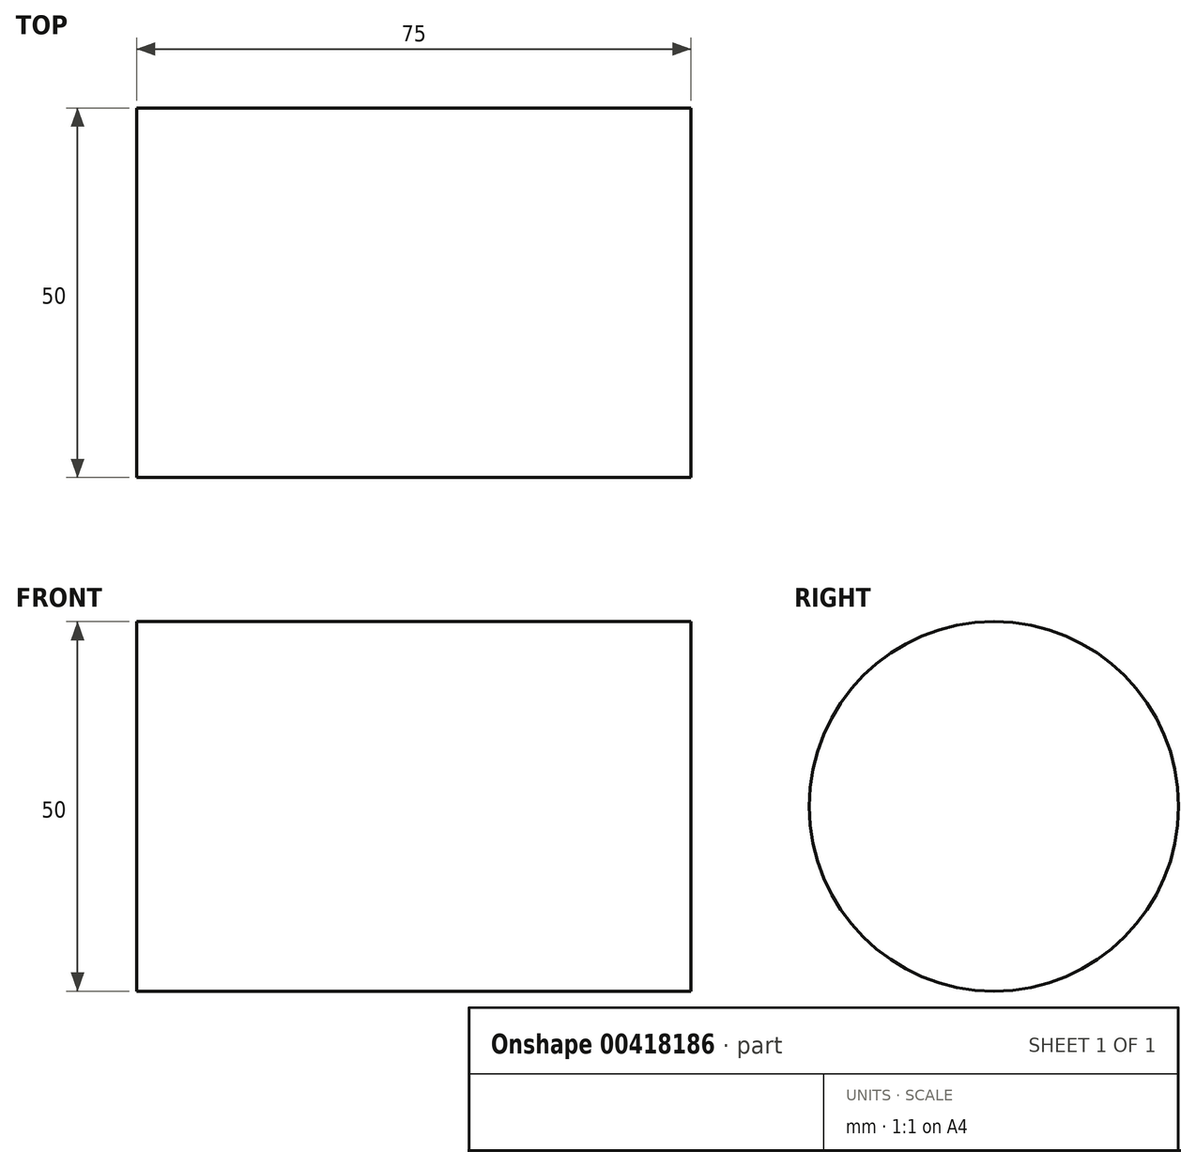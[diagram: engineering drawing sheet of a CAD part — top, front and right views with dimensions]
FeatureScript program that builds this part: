
annotation { "Feature Type Name" : "Feature", "Feature Type Description" : "" }
export const myFeature = defineFeature(function(context is Context, id is Id, definition is map)
    precondition{}
    {
        {
            var Q0;
            Q0=qCreatedBy(makeId("Right.planeOp"),FACE);
            var sketch = newSketch(context, id + "F0", { "sketchPlane" : qUnion([Q0])});
            skCircle(sketch, "E0", {"center": v(0, 0) * mm, "radius": 25 * mm});
            skSolve(sketch);
        }
        {
            var Q0;
            Q0 = qSketchRegion(id + "F0", true);
            extrude(context, id + "F1", {"entities" : qUnion([Q0]), "depth" : 75 * mm});
        }
    });
